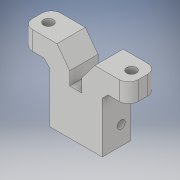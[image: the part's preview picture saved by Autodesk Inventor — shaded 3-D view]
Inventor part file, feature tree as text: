
AUTODESK INVENTOR PART (.ipt)
format: ipt  version: 2018 (Build 220112000, 112)  size: 205,824 bytes
history: native  units: in
note: dims shown in document units (in); Inventor stores cm internally (conversion verified against a paired STEP export)
features: extrude x8, sketch x8, mirror x1, fillet x1, chamfer x1, projected_geometry x1
ambient origin geometry x8: Origin, YZ Plane, XZ Plane, XY Plane, X Axis, Y Axis, Z Axis, Center Point
bodies: Solid1 (feature_tree)
feature tree (20):
  extrude  "Extrusion1"  Depth=1.1811in
  extrude  "Extrusion2"  Depth=0.1575in
  extrude  "Extrusion3"  Depth=0.3937in
  mirror  "Mirror1"
  extrude  "Extrusion4"  Depth=0.2362in
  fillet  "Fillet1"  Radius=0.2362in
  chamfer  "Chamfer1"  Distance=0.3937in
  extrude  "Extrusion7"  Depth=0.1969in TaperAngle=0.0deg
  extrude  "Extrusion8"  Depth=0.3228in
  extrude  "Extrusion5"  Depth=0.3937in
  extrude  "Extrusion9"  Depth=0.1969in TaperAngle=0.0deg
  sketch  "Sketch1"  dims[d0=0.7874in d1=1.1811in]
  sketch  "Sketch2"  dims[d2=0.1575in d3=0.1575in]
  sketch  "Sketch3"  dims[d4=0.5512in d5=0.3937in]
  sketch  "Sketch4"  dims[d6=0.5906in d7=0.0in d8=0.2047in d9=0.2362in]
  sketch  "Sketch6"  dims[d10=0.2362in d11=0.3937in d12=0.0in]
  sketch  "Sketch8"  dims[d13=0.3228in d17=0.1969in d18=0.0in]
  sketch  "Sketch9"  dims[d22=0.3504in d23=0.3228in]
  sketch  "Sketch11"  dims[d24=0.1654in d25=0.3937in d27=0.1969in d28=0.0in d29=0.2559in d30=0.7874in d32=0.1969in d33=0.0in d37=0.1969in d38=0.1181in d39=0.0787in d40=45.0deg d41=0.1181in d42=0.0in d44=0.7874in d45=0.1181in d46=0.0in d47=0.3543in d48=0.1575in d49=0.1654in d50=0.1181in d51=0.0in]
  projected_geometry  "Projected Loop1"
